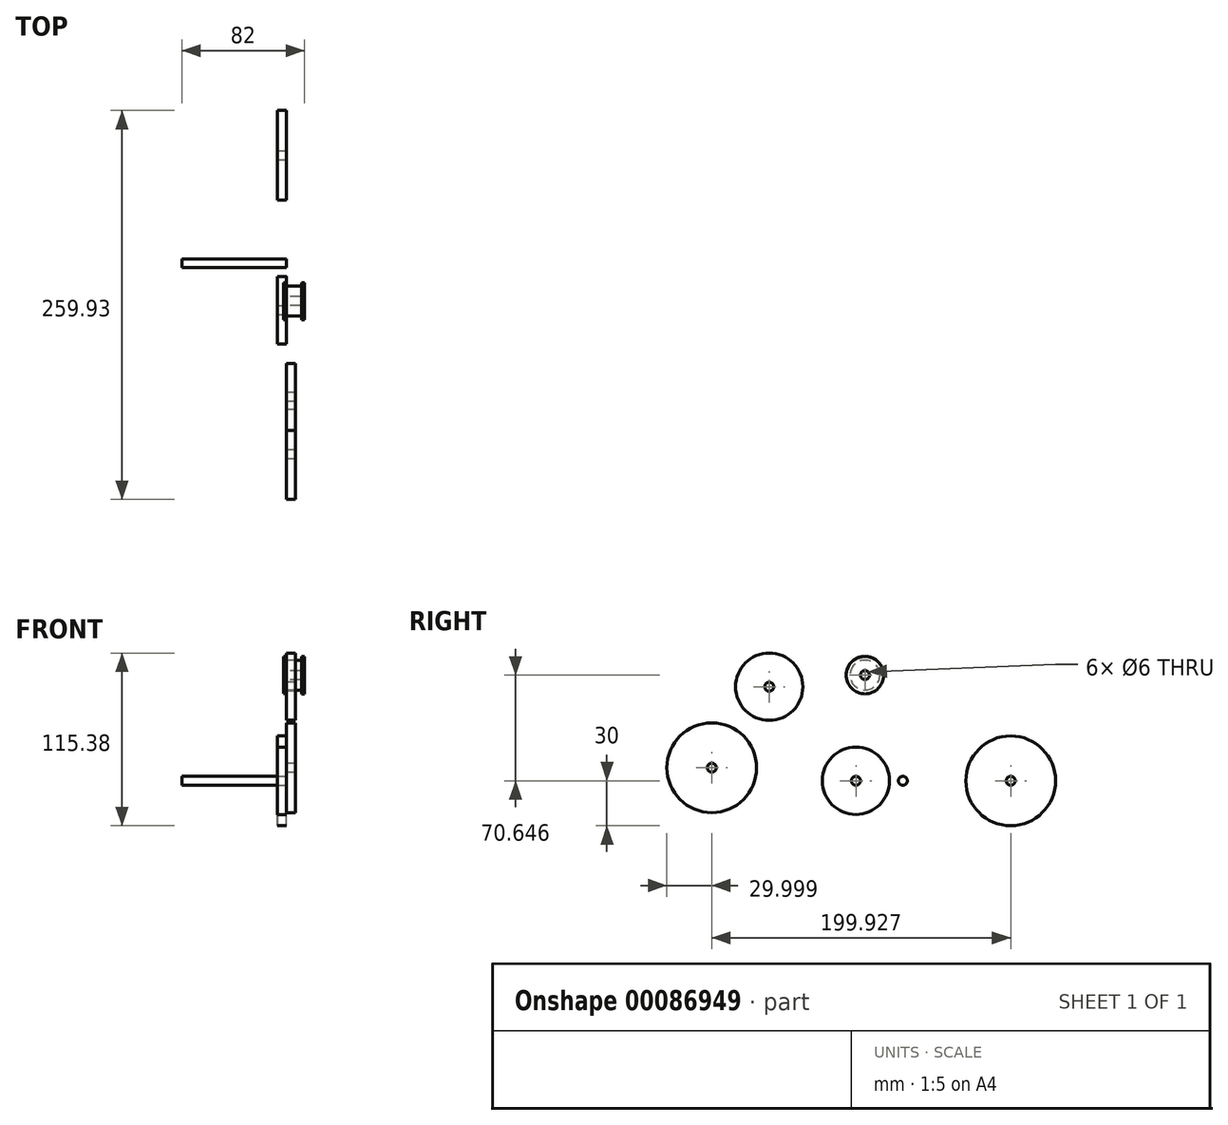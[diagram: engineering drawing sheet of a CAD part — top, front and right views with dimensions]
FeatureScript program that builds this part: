
annotation { "Feature Type Name" : "Feature", "Feature Type Description" : "" }
export const myFeature = defineFeature(function(context is Context, id is Id, definition is map)
    precondition{}
    {
        {
            var Q0;
            Q0=qCreatedBy(makeId("Right.planeOp"),FACE);
            var sketch = newSketch(context, id + "F0", { "sketchPlane" : qUnion([Q0])});
            skCircle(sketch, "E0", {"center": v(0, 0) * mm, "radius": 22.5 * mm});
            skSolve(sketch);
        }
        {
            var Q0;
            Q0=makeQuery(id+"F0.imprint","IMPRINT",FACE,{"disambiguationData":[TD([[makeQuery(id+"F0.imprint","IMPRINT",EDGE,{"derivedFrom":sQuery(id+"F0.wireOp",EDGE,"E0")}),1.0]])]});
            extrude(context, id + "F1", {"entities" : qUnion([Q0]), "oppositeDirection" : true, "depth" : 6 * mm});
        }
        {
            var Q0;
            Q0=sQuery(id+"F0.wireOp",VERTEX,"E0.center");
            var Q1;
            Q1=makeQuery(id+"F1.opExtrude","SWEPT_BODY",BODY,{"disambiguationData":[OSD([sQuery(id+"F0.wireOp",EDGE,"E0")])]});
            hole(context, id + "F2", {"style" : HoleStyle.SIMPLE, "endStyle" : HoleEndStyle.THROUGH, "holeDiameter" : 6 * mm, "startFromSketch" : true, "locations" : qUnion([Q0]), "scope" : qUnion([Q1]), "isTappedThrough" : true});
        }
        {
            var Q0;
            Q0=qCreatedBy(makeId("Right.planeOp"),FACE);
            var sketch = newSketch(context, id + "F3", { "sketchPlane" : qUnion([Q0])});
            skCircle(sketch, "E1", {"center": v(103.52, 0) * mm, "radius": 30 * mm});
            skSolve(sketch);
        }
        {
            var Q0;
            Q0=makeQuery(id+"F3.imprint","IMPRINT",FACE,{"disambiguationData":[TD([[makeQuery(id+"F3.imprint","IMPRINT",EDGE,{"derivedFrom":sQuery(id+"F3.wireOp",EDGE,"E1")}),1.0]])]});
            extrude(context, id + "F4", {"entities" : qUnion([Q0]), "oppositeDirection" : true, "depth" : 6 * mm});
        }
        {
            var Q0;
            Q0=sQuery(id+"F3.wireOp",VERTEX,"E1.center");
            var Q1;
            Q1=makeQuery(id+"F4.opExtrude","SWEPT_BODY",BODY,{"disambiguationData":[OSD([sQuery(id+"F3.wireOp",EDGE,"E1")])]});
            hole(context, id + "F5", {"style" : HoleStyle.SIMPLE, "endStyle" : HoleEndStyle.THROUGH, "holeDiameter" : 6 * mm, "startFromSketch" : true, "locations" : qUnion([Q0]), "scope" : qUnion([Q1]), "isTappedThrough" : true});
        }
        {
            var Q0;
            Q0=qCreatedBy(makeId("Right.planeOp"),FACE);
            var sketch = newSketch(context, id + "F6", { "sketchPlane" : qUnion([Q0])});
            skCircle(sketch, "E2", {"center": v(31.4, 0) * mm, "radius": 3 * mm});
            skSolve(sketch);
        }
        {
            var Q0;
            Q0=makeQuery(id+"F6.imprint","IMPRINT",FACE,{"disambiguationData":[TD([[makeQuery(id+"F6.imprint","IMPRINT",EDGE,{"derivedFrom":sQuery(id+"F6.wireOp",EDGE,"E2")}),1.0]])]});
            extrude(context, id + "F7", {"entities" : qUnion([Q0]), "oppositeDirection" : true, "depth" : 70 * mm});
        }
        {
            var Q0;
            Q0=qCreatedBy(makeId("Right.planeOp"),FACE);
            var sketch = newSketch(context, id + "F8", { "sketchPlane" : qUnion([Q0])});
            skCircle(sketch, "E3", {"center": v(-96.41, 8.72) * mm, "radius": 30 * mm});
            skSolve(sketch);
        }
        {
            var Q0;
            Q0=makeQuery(id+"F8.imprint","IMPRINT",FACE,{"disambiguationData":[TD([[makeQuery(id+"F8.imprint","IMPRINT",EDGE,{"derivedFrom":sQuery(id+"F8.wireOp",EDGE,"E3")}),1.0]])]});
            extrude(context, id + "F9", {"entities" : qUnion([Q0]), "depth" : 6 * mm});
        }
        {
            var Q0;
            Q0=sQuery(id+"F8.wireOp",VERTEX,"E3.center");
            var Q1;
            Q1=makeQuery(id+"F9.opExtrude","SWEPT_BODY",BODY,{"disambiguationData":[OSD([sQuery(id+"F8.wireOp",EDGE,"E3")])]});
            hole(context, id + "F10", {"style" : HoleStyle.SIMPLE, "endStyle" : HoleEndStyle.THROUGH, "oppositeDirection" : true, "holeDiameter" : 6 * mm, "startFromSketch" : true, "locations" : qUnion([Q0]), "scope" : qUnion([Q1]), "isTappedThrough" : true});
        }
        {
            var Q0;
            Q0=qCreatedBy(makeId("Right.planeOp"),FACE);
            var sketch = newSketch(context, id + "F11", { "sketchPlane" : qUnion([Q0])});
            skCircle(sketch, "E4", {"center": v(-57.96, 62.88) * mm, "radius": 22.5 * mm});
            skSolve(sketch);
        }
        {
            var Q0;
            Q0=makeQuery(id+"F11.imprint","IMPRINT",FACE,{"disambiguationData":[TD([[makeQuery(id+"F11.imprint","IMPRINT",EDGE,{"derivedFrom":sQuery(id+"F11.wireOp",EDGE,"E4")}),1.0]])]});
            extrude(context, id + "F12", {"entities" : qUnion([Q0]), "depth" : 6 * mm});
        }
        {
            var Q0;
            Q0=sQuery(id+"F11.wireOp",VERTEX,"E4.center");
            var Q1;
            Q1=makeQuery(id+"F12.opExtrude","SWEPT_BODY",BODY,{"disambiguationData":[OSD([sQuery(id+"F11.wireOp",EDGE,"E4")])]});
            hole(context, id + "F13", {"style" : HoleStyle.SIMPLE, "endStyle" : HoleEndStyle.THROUGH, "oppositeDirection" : true, "holeDiameter" : 6 * mm, "startFromSketch" : true, "locations" : qUnion([Q0]), "scope" : qUnion([Q1]), "isTappedThrough" : true});
        }
        {
            var Q0;
            Q0=qCreatedBy(makeId("Right.planeOp"),FACE);
            var sketch = newSketch(context, id + "F14", { "sketchPlane" : qUnion([Q0])});
            skCircle(sketch, "E5", {"center": v(6.05, 70.65) * mm, "radius": 10 * mm});
            skSolve(sketch);
        }
        {
            var Q0;
            Q0=makeQuery(id+"F14.imprint","IMPRINT",FACE,{"disambiguationData":[TD([[makeQuery(id+"F14.imprint","IMPRINT",EDGE,{"derivedFrom":sQuery(id+"F14.wireOp",EDGE,"E5")}),1.0]])]});
            extrude(context, id + "F15", {"entities" : qUnion([Q0]), "depth" : 10 * mm});
        }
        {
            var Q0;
            Q0=sQuery(id+"F14.wireOp",VERTEX,"E5.center");
            var Q1;
            Q1=makeQuery(id+"F15.opExtrude","SWEPT_BODY",BODY,{"disambiguationData":[OSD([sQuery(id+"F14.wireOp",EDGE,"E5")])]});
            hole(context, id + "F16", {"style" : HoleStyle.SIMPLE, "endStyle" : HoleEndStyle.THROUGH, "oppositeDirection" : true, "holeDiameter" : 6 * mm, "startFromSketch" : true, "locations" : qUnion([Q0]), "scope" : qUnion([Q1]), "isTappedThrough" : true});
        }
        {
            var Q0;
            Q0=makeQuery(id+"F15.opExtrude","CAP_FACE",FACE,{"disambiguationData":[OSD([sQuery(id+"F14.wireOp",EDGE,"E5")])],"isStart":false});
            var sketch = newSketch(context, id + "F17", { "sketchPlane" : qUnion([Q0])});
            skCircle(sketch, "E6", {"center": v(6.05, 70.65) * mm, "radius": 12.5 * mm});
            skSolve(sketch);
        }
        {
            var Q0;
            Q0=makeQuery(id+"F17.imprint","IMPRINT",FACE,{"disambiguationData":[TD([[makeQuery(id+"F17.imprint","IMPRINT",EDGE,{"derivedFrom":sQuery(id+"F17.wireOp",EDGE,"E6")}),1.0]])]});
            var Q1;
            {var subQ0=sQuery(id+"F14.wireOp",EDGE,"E5");Q1=makeQuery(id+"F17.imprint","IMPRINT",FACE,{"disambiguationData":[TD([[makeQuery(id+"F17.imprint","IMPRINT",EDGE,{"derivedFrom":makeQuery(id+"F15.opExtrude","CAP_EDGE",EDGE,{"disambiguationData":[OSD([subQ0])],"isStart":false})}),1.0]])]});}
            extrude(context, id + "F18", {"entities" : qUnion([Q0, Q1]), "depth" : 2 * mm});
        }
        {
            var Q0;
            Q0=makeQuery(id+"F14.imprint","IMPRINT",FACE,{"disambiguationData":[TD([[makeQuery(id+"F14.imprint","IMPRINT",EDGE,{"derivedFrom":sQuery(id+"F14.wireOp",EDGE,"E5")}),1.0]])]});
            var sketch = newSketch(context, id + "F19", { "sketchPlane" : qUnion([Q0])});
            skCircle(sketch, "E7", {"center": v(6.04, 70.68) * mm, "radius": 12.5 * mm});
            skSolve(sketch);
        }
        {
            var Q0;
            Q0=makeQuery(id+"F19.imprint","IMPRINT",FACE,{"disambiguationData":[TD([[makeQuery(id+"F19.imprint","IMPRINT",EDGE,{"derivedFrom":sQuery(id+"F19.wireOp",EDGE,"E7")}),1.0]])]});
            var Q1;
            Q1=makeQuery(id+"F14.imprint","IMPRINT",FACE,{"disambiguationData":[TD([[makeQuery(id+"F14.imprint","IMPRINT",EDGE,{"derivedFrom":sQuery(id+"F14.wireOp",EDGE,"E5")}),1.0]])]});
            extrude(context, id + "F20", {"entities" : qUnion([Q0, Q1]), "operationType" : NewBodyOperationType.ADD, "oppositeDirection" : true, "depth" : 2 * mm});
        }
        {
            var Q0;
            Q0=sQuery(id+"F14.wireOp",VERTEX,"E5.center");
            var Q1;
            Q1=makeQuery(id+"F15.opExtrude","SWEPT_BODY",BODY,{"disambiguationData":[OSD([sQuery(id+"F14.wireOp",EDGE,"E5")])]});
            hole(context, id + "F21", {"style" : HoleStyle.SIMPLE, "endStyle" : HoleEndStyle.THROUGH, "holeDiameter" : 6 * mm, "startFromSketch" : true, "locations" : qUnion([Q0]), "scope" : qUnion([Q1]), "isTappedThrough" : true});
        }
    });
